# Revit family: Corner_Shelf-Grohe-BauCosmopolitan-40663001
name_source: partatom
category: Specialty Equipment
revit_build: Autodesk Revit 2014 (Build: 20130308_1515(x64)
units: mm (PartAtom-declared; Revit-internal decimal feet)

## types (1)
- 40663001
    Assembly Code = C1030200
    Default Elevation = 1016 mm
    Description = BauCosmopolitan Large corner basket
    Finish = Metal-Grohe-001-Chrome
    Height = 32 mm
    Installation Type = Wall Mounted
    Length = 164 mm
    Manufacturer = Grohe
    Material = Metal-Grohe-001-Chrome
    Model = 40663001
    Price = Prices may vary. Please consult Manufacturer Representative for most up-to-date price list.
    Product Page URL = https://www.grohe.ca
    URL = https://www.grohe.us
    Width = 233 mm  [stored 0.764436 ft]

note: [stored X ft] marks values corroborated as IEEE doubles in the binary element streams (Revit-internal decimal feet)

## geometry (parser evidence)
native form markers: Sweep x4
no freeform markers — native parametric forms only
